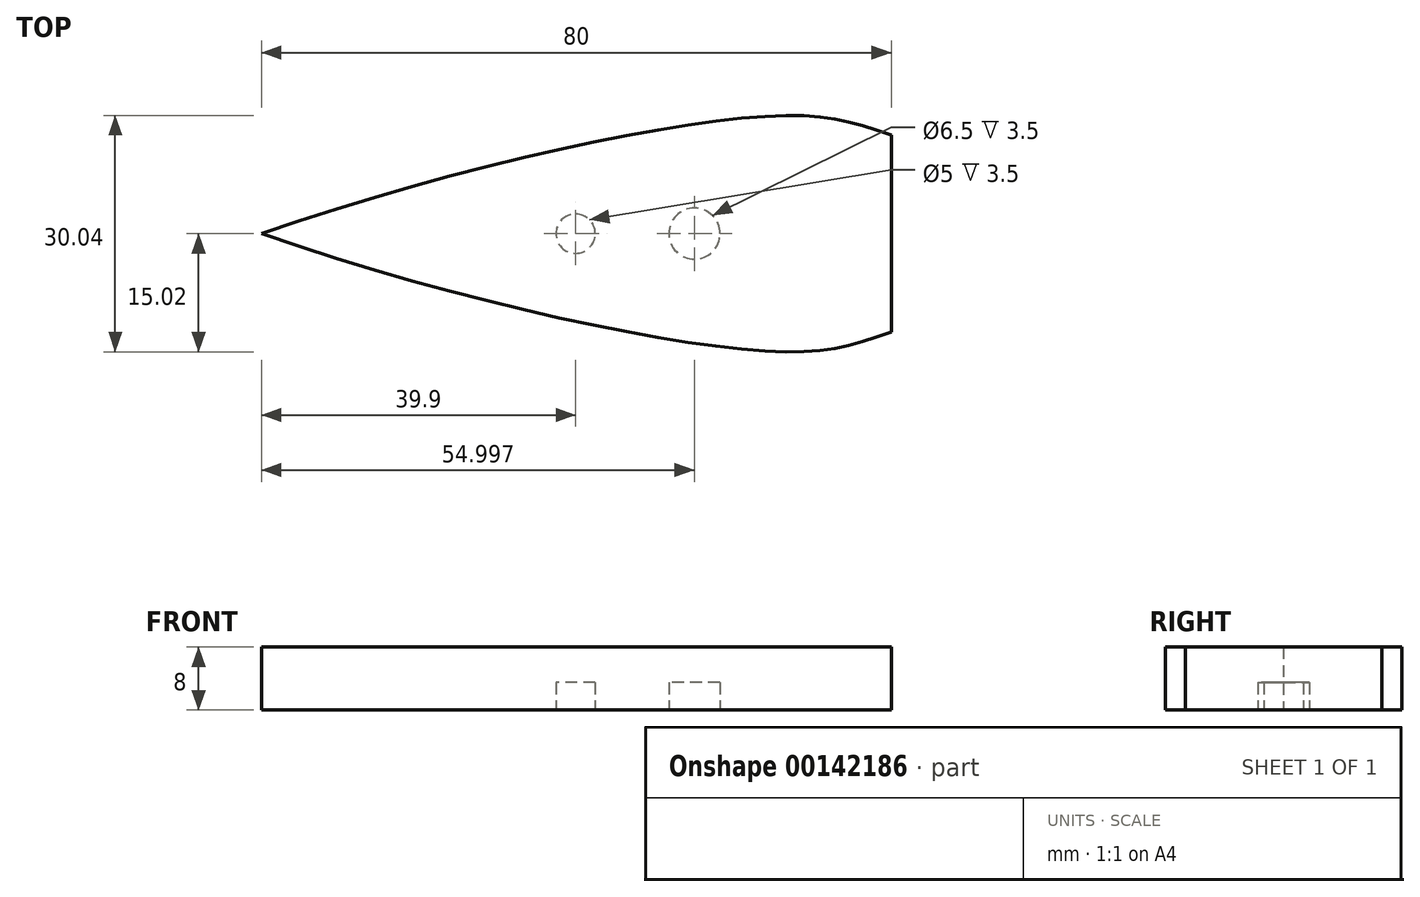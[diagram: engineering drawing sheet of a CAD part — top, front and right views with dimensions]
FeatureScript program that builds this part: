
annotation { "Feature Type Name" : "Feature", "Feature Type Description" : "" }
export const myFeature = defineFeature(function(context is Context, id is Id, definition is map)
    precondition{}
    {
        {
            var Q0;
            Q0=qCreatedBy(makeId("Top.planeOp"),FACE);
            var sketch = newSketch(context, id + "F0", { "sketchPlane" : qUnion([Q0])});
            skLineSegment(sketch, "E0", {"start": v(-67.38, 0) * mm, "end": v(87.29, 0) * mm, "construction": true});
            skLineSegment(sketch, "E1", {"start": v(26.16, 15) * mm, "end": v(26.16, 0) * mm, "construction": true});
            skFitSpline(sketch, "E2", {"points": [v(-39.9, 0) * mm, v(26.16, 15) * mm, v(40.1, 12.5) * mm], "startDerivative": vector(108.22, 37.52) * mm, "endDerivative": vector(45.71, -15.8) * mm});
            skLineSegment(sketch, "E3", {"start": v(40.1, 12.5) * mm, "end": v(40.1, 0) * mm});
            skCircle(sketch, "E4", {"center": v(0, 0) * mm, "radius": 2.5 * mm});
            skFitSpline(sketch, "E5.MirrorCS", {"points": [v(-39.9, 0) * mm, v(26.16, -15) * mm, v(40.1, -12.5) * mm], "startDerivative": vector(108.22, -37.52) * mm, "endDerivative": vector(45.71, 15.8) * mm});
            skLineSegment(sketch, "E6.MirrorCS", {"start": v(40.1, -12.5) * mm, "end": v(40.1, 0) * mm});
            skCircle(sketch, "E7", {"center": v(15.1, 0) * mm, "radius": 3.25 * mm});
            skSolve(sketch);
        }
        {
            var Q0;
            Q0=makeQuery(id+"F0.imprint","IMPRINT",FACE,{"disambiguationData":[TD([[makeQuery(id+"F0.imprint","IMPRINT",EDGE,{"derivedFrom":sQuery(id+"F0.wireOp",EDGE,"E2")}),-1.0]])]});
            var Q1;
            Q1=makeQuery(id+"F0.imprint","IMPRINT",FACE,{"disambiguationData":[TD([[makeQuery(id+"F0.imprint","IMPRINT",EDGE,{"derivedFrom":sQuery(id+"F0.wireOp",EDGE,"E4")}),1.0]])]});
            var Q2;
            Q2=makeQuery(id+"F0.imprint","IMPRINT",FACE,{"disambiguationData":[TD([[makeQuery(id+"F0.imprint","IMPRINT",EDGE,{"derivedFrom":sQuery(id+"F0.wireOp",EDGE,"E7")}),1.0]])]});
            extrude(context, id + "F1", {"entities" : qUnion([Q0, Q1, Q2]), "depth" : 8 * mm, "offsetDistance" : 25 * mm});
        }
        {
            var Q0;
            Q0=makeQuery(id+"F0.imprint","IMPRINT",FACE,{"disambiguationData":[TD([[makeQuery(id+"F0.imprint","IMPRINT",EDGE,{"derivedFrom":sQuery(id+"F0.wireOp",EDGE,"E4")}),1.0]])]});
            var Q1;
            Q1=makeQuery(id+"F0.imprint","IMPRINT",FACE,{"disambiguationData":[TD([[makeQuery(id+"F0.imprint","IMPRINT",EDGE,{"derivedFrom":sQuery(id+"F0.wireOp",EDGE,"E7")}),1.0]])]});
            extrude(context, id + "F2", {"entities" : qUnion([Q0, Q1]), "operationType" : NewBodyOperationType.REMOVE, "depth" : 3.5 * mm, "offsetDistance" : 25 * mm});
        }
    });
